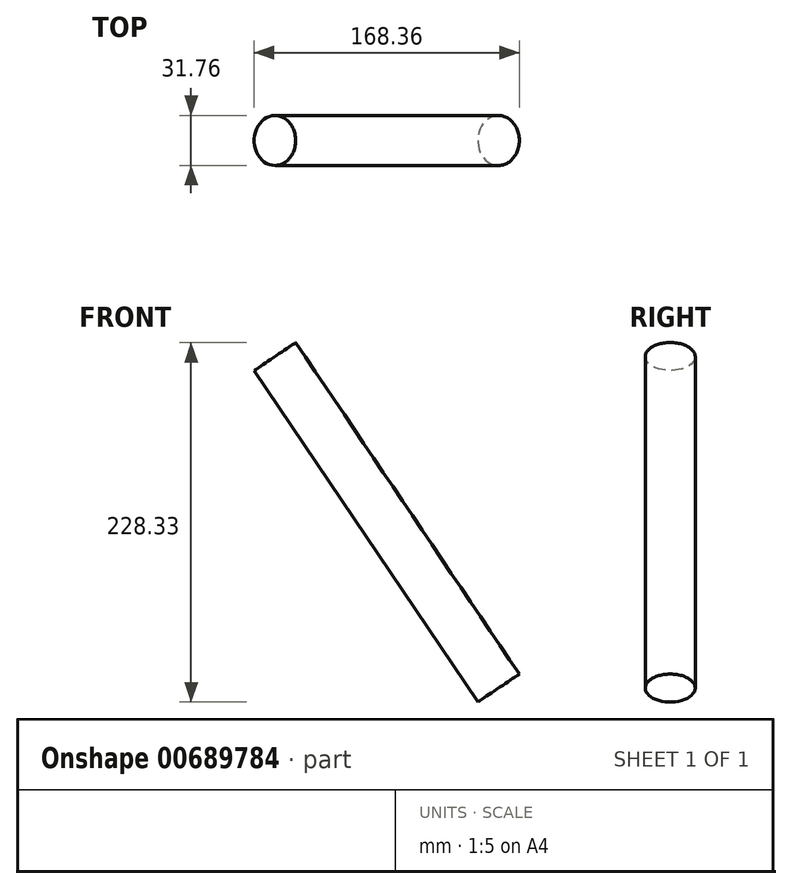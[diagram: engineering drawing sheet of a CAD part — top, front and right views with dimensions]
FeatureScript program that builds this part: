
annotation { "Feature Type Name" : "Feature", "Feature Type Description" : "" }
export const myFeature = defineFeature(function(context is Context, id is Id, definition is map)
    precondition{}
    {
        {
            var Q0;
            Q0=qCreatedBy(makeId("Front.planeOp"),FACE);
            var sketch = newSketch(context, id + "F0", { "sketchPlane" : qUnion([Q0])});
            skLineSegment(sketch, "E0", {"start": v(0, 0) * mm, "end": v(-142.03, 210.58) * mm});
            skSolve(sketch);
        }
        {
            var Q0;
            Q0=sQuery(id+"F0.wireOp",VERTEX,"E0.end");
            var Q1;
            Q1=sQuery(id+"F0.wireOp",EDGE,"E0");
            cPlane(context, id + "F1", {"entities" : qUnion([Q0, Q1]), "cplaneType" : CPlaneType.LINE_POINT, "offset" : 25.4 * mm, "width" : 152.4 * mm, "height" : 152.4 * mm});
        }
        {
            var Q0;
            Q0=qCreatedBy(id+"F1.planeOp",FACE);
            var sketch = newSketch(context, id + "F2", { "sketchPlane" : qUnion([Q0])});
            skCircle(sketch, "E1", {"center": v(0, 0) * mm, "radius": 15.88 * mm});
            skSolve(sketch);
        }
        {
            var Q0;
            Q0=makeQuery(id+"F2.imprint","IMPRINT",FACE,{"disambiguationData":[TD([[makeQuery(id+"F2.imprint","IMPRINT",EDGE,{"derivedFrom":sQuery(id+"F2.wireOp",EDGE,"E1")}),1.0]])]});
            extrude(context, id + "F3", {"entities" : qUnion([Q0]), "oppositeDirection" : true, "depth" : 254 * mm, "offsetDistance" : 25.4 * mm});
        }
    });
